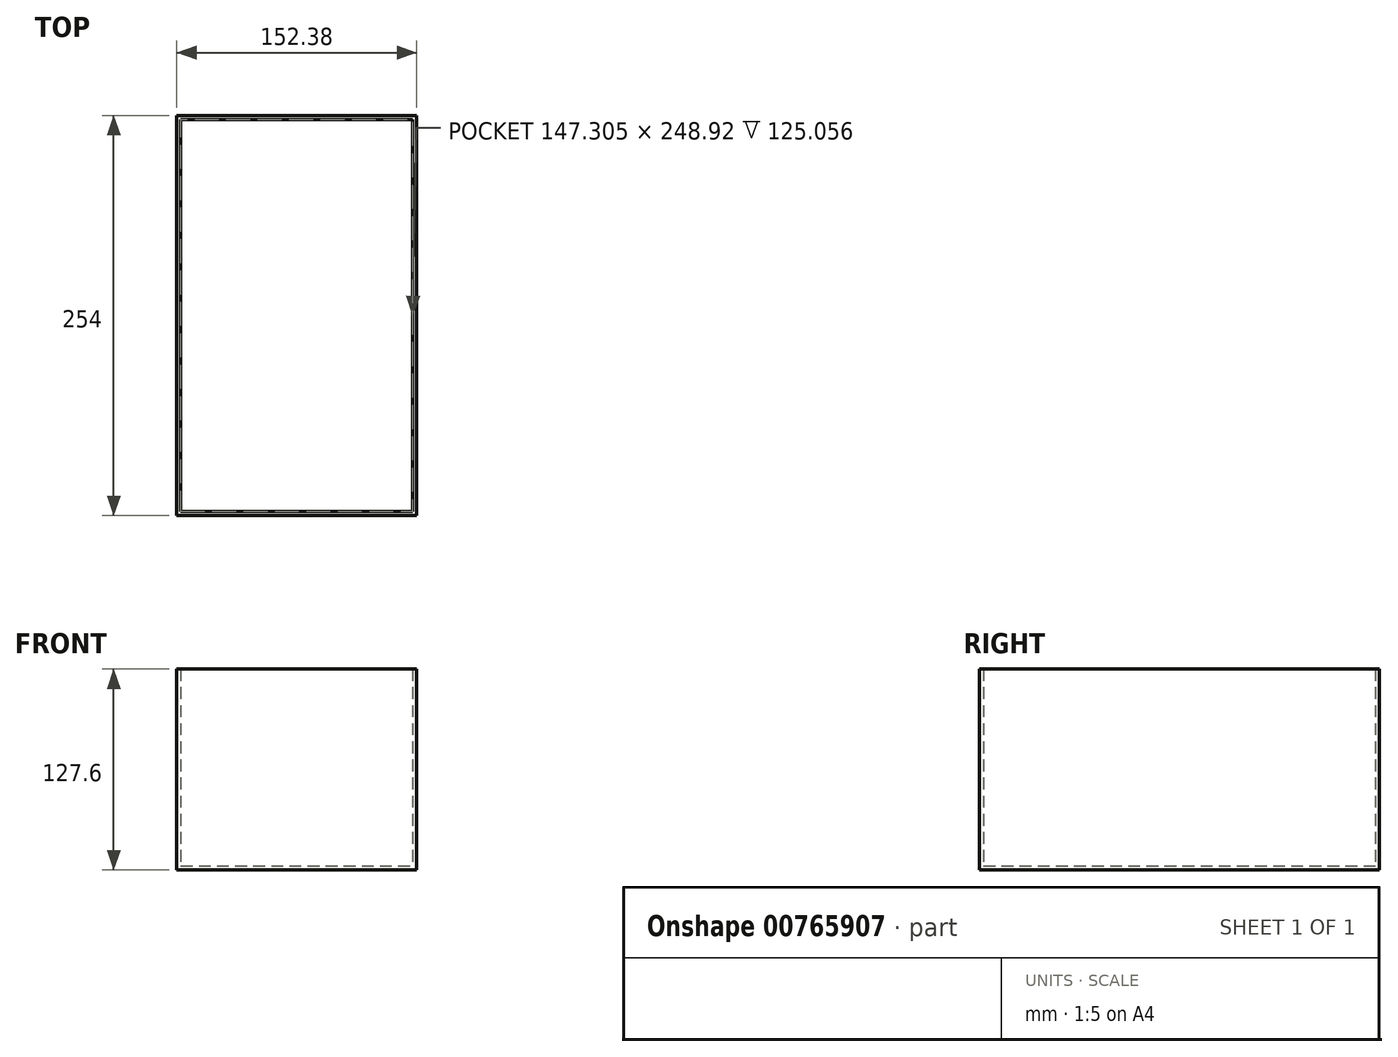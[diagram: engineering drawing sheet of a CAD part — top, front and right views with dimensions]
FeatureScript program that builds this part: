
annotation { "Feature Type Name" : "Feature", "Feature Type Description" : "" }
export const myFeature = defineFeature(function(context is Context, id is Id, definition is map)
    precondition{}
    {
        {
            var Q0;
            Q0=qCreatedBy(makeId("Front.planeOp"),FACE);
            var sketch = newSketch(context, id + "F0", { "sketchPlane" : qUnion([Q0])});
            skLineSegment(sketch, "E0.bottom", {"start": v(-76.2, 76.5) * mm, "end": v(76.2, 76.5) * mm});
            skLineSegment(sketch, "E0.top", {"start": v(-76.2, -76.5) * mm, "end": v(76.2, -76.5) * mm});
            skLineSegment(sketch, "E0.left", {"start": v(-76.2, 76.5) * mm, "end": v(-76.2, -76.5) * mm});
            skLineSegment(sketch, "E0.right", {"start": v(76.2, 76.5) * mm, "end": v(76.2, -76.5) * mm});
            skPoint(sketch, "E0.middle", {"position": v(0, 0) * mm});
            skSolve(sketch);
        }
        {
            var Q0;
            Q0=makeQuery(id+"F0.imprint","IMPRINT",FACE,{"disambiguationData":[TD([[makeQuery(id+"F0.imprint","IMPRINT",EDGE,{"derivedFrom":sQuery(id+"F0.wireOp",EDGE,"E0.bottom")}),-1.0]])]});
            extrude(context, id + "F1", {"entities" : qUnion([Q0]), "depth" : 254 * mm, "offsetDistance" : 25.4 * mm});
        }
        {
            var Q0;
            Q0=makeQuery(id+"F1.opExtrude","SWEPT_FACE",FACE,{"disambiguationData":[OSD([sQuery(id+"F0.wireOp",EDGE,"E0.bottom")])]});
            var sketch = newSketch(context, id + "F2", { "sketchPlane" : qUnion([Q0])});
            skSolve(sketch);
        }
        {
            var Q0;
            {var subQ0=sQuery(id+"F0.wireOp",EDGE,"E0.bottom");Q0=makeQuery(id+"F2.imprint","IMPRINT",FACE,{"disambiguationData":[TD([[makeQuery(id+"F2.imprint","IMPRINT",EDGE,{"derivedFrom":makeQuery(id+"F1.opExtrude","CAP_EDGE",EDGE,{"disambiguationData":[OSD([subQ0])],"isStart":true})}),-1.0]])]});}
            extrude(context, id + "F3", {"entities" : qUnion([Q0]), "operationType" : NewBodyOperationType.REMOVE, "oppositeDirection" : true, "depth" : 25.4 * mm, "offsetDistance" : 25.4 * mm});
        }
        {
            var Q0;
            Q0=makeQuery(id+"F3.boolean.opBoolean","COPY",FACE,{"derivedFrom":makeQuery(id+"F3.opExtrude","CAP_FACE",FACE,{"disambiguationData":[OSD([sQuery(id+"F0.wireOp",EDGE,"E0.bottom"),sQuery(id+"F0.wireOp",EDGE,"E0.left"),sQuery(id+"F0.wireOp",EDGE,"E0.right")])],"isStart":false})});
            shell(context, id + "F4", {"entities" : qUnion([Q0]), "thickness" : 2.54 * mm});
        }
    });
